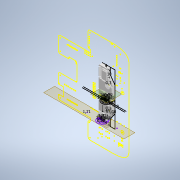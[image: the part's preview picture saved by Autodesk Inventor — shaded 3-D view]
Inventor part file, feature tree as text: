
AUTODESK INVENTOR PART (.ipt)
format: ipt  version: 2022 (Build 260153000, 153)  size: 899,072 bytes
history: native  units: mm
features: sketch x17, extrude x14, reference x14, other x12, fillet x8, projected_geometry x8, mirror x5, chamfer x2
ambient origin geometry x8: Origin, YZ Plane, XZ Plane, XY Plane, X Axis, Y Axis, Z Axis, Center Point
bodies: Body1 (feature_tree)
feature tree (80):
  other  "Твердое тело1"
  sketch  "Эскиз1"
  other  "РабПлоскость1"
  extrude  "Выдавливание1"  Depth=0.3mm
  extrude  "Выдавливание2"  Depth=0.3mm
  chamfer  "Фаска1"  Distance=4.0mm
  extrude  "Выдавливание3"  Depth=10.0mm
  fillet  "Сопряжение1"  Radius=4.0mm
  sketch  "Эскиз5"
  extrude  "Выдавливание4"  Depth=10.0mm
  extrude  "Выдавливание5"  Depth=27.0mm
  extrude  "Выдавливание6"  Depth=6.0mm
  extrude  "Выдавливание7"  Depth=4.0mm
  mirror  "Зеркальное отражение1"
  other  "РабПлоскость2"
  sketch  "Эскиз10"
  extrude  "Выдавливание8"  Depth=4.0mm
  extrude  "Выдавливание9"  Depth=4.0mm
  extrude  "Выдавливание10"  Depth=6.108652mm
  fillet  "Сопряжение2"  Radius=8.0mm
  fillet  "Сопряжение3"  Radius=6.0mm
  fillet  "Сопряжение4"  Radius=4.0mm
  fillet  "Сопряжение6"  Radius=4.0mm
  mirror  "Зеркальное отражение2"
  mirror  "Зеркальное отражение3"
  extrude  "Выдавливание11"  Depth=10.0mm
  other  "РабПлоскость3"
  extrude  "Выдавливание12"  Depth=4.0mm
  chamfer  "Фаска2"  Distance=3.0mm
  fillet  "Сопряжение7"  Radius=3.2mm
  extrude  "Выдавливание13"  Depth=3.2mm
  extrude  "Выдавливание14"  Depth=3.0mm TaperAngle=0.0deg
  mirror  "Зеркальное отражение4"
  mirror  "Зеркальное отражение5"
  fillet  "Сопряжение8"  Radius=2.0mm
  fillet  "Сопряжение9"  Radius=0.5mm
  reference  "Ссылка1"
  reference  "Ссылка2"
  reference  "Ссылка3"
  sketch  "Эскиз2"
  sketch  "Эскиз3"
  projected_geometry  "Спроецированная петля1"
  sketch  "Эскиз4"
  reference  "Ссылка4"
  reference  "Ссылка5"
  reference  "Ссылка6"
  reference  "Ссылка7"
  projected_geometry  "Спроецированная петля2"
  reference  "Ссылка8"
  reference  "Ссылка9"
  sketch  "Эскиз6"
  sketch  "Эскиз7"
  sketch  "Эскиз8"
  sketch  "Эскиз9"
  projected_geometry  "Спроецированная петля3"
  reference  "Ссылка10"
  sketch  "Эскиз11"
  sketch  "Эскиз12"
  sketch  "Эскиз13"
  sketch  "Эскиз14"
  reference  "Ссылка11"
  reference  "Ссылка12"
  reference  "Ссылка13"
  reference  "Ссылка14"
  sketch  "Эскиз15"
  projected_geometry  "Спроецированная петля4"
  projected_geometry  "Спроецированная петля5"
  sketch  "Эскиз16"
  projected_geometry  "Спроецированная петля6"
  sketch  "Эскиз17"
  projected_geometry  "Спроецированная петля7"
  projected_geometry  "Спроецированная петля8"
  other  "<userpath>\Documents\Git\MZCAT_2024_construction\MZCAT_2024_RPI_2\MZCAT_4.iam"
  other  "MZCAT_4.iam"
  other  "MZCAT_motherboard_fnl:1"
  other  "soldered nut_1,5:1"
  other  "soldered nut_1,5:2"
  other  "diffuser:1"
  other  "motherboard_plate:1"
  other  "motherboard_fixator:1"
